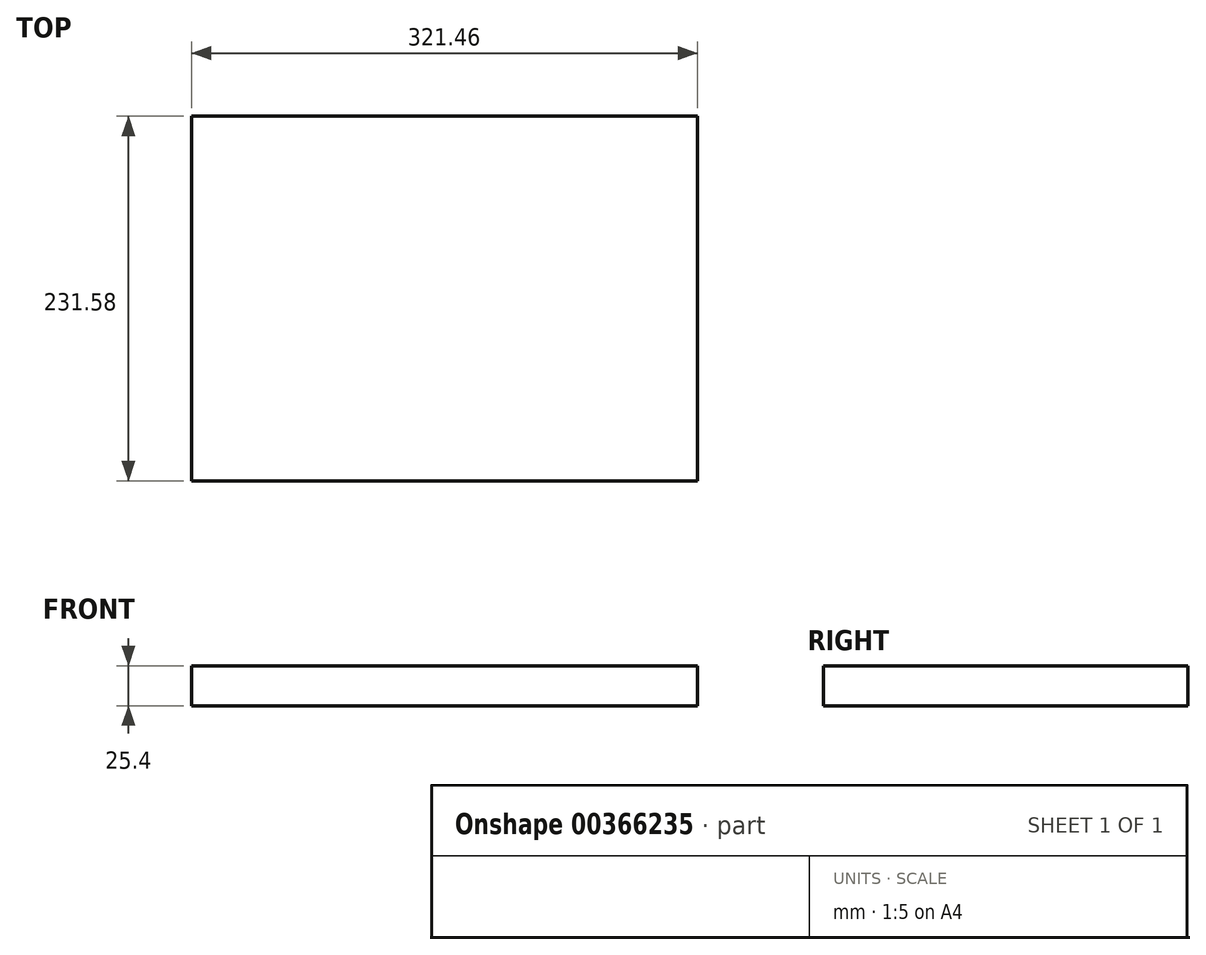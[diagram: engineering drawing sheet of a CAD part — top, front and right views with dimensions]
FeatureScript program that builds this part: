
annotation { "Feature Type Name" : "Feature", "Feature Type Description" : "" }
export const myFeature = defineFeature(function(context is Context, id is Id, definition is map)
    precondition{}
    {
        {
            var Q0;
            Q0=qCreatedBy(makeId("Top.planeOp"),FACE);
            var sketch = newSketch(context, id + "F0", { "sketchPlane" : qUnion([Q0])});
            skLineSegment(sketch, "E0.bottom", {"start": v(-75.95, 128.57) * mm, "end": v(245.51, 128.57) * mm});
            skLineSegment(sketch, "E0.top", {"start": v(-75.95, -103.01) * mm, "end": v(245.51, -103.01) * mm});
            skLineSegment(sketch, "E0.left", {"start": v(-75.95, 128.57) * mm, "end": v(-75.95, -103.01) * mm});
            skLineSegment(sketch, "E0.right", {"start": v(245.51, 128.57) * mm, "end": v(245.51, -103.01) * mm});
            skSolve(sketch);
        }
        {
            var Q0;
            Q0 = qSketchRegion(id + "F0", true);
            extrude(context, id + "F1", {"entities" : qUnion([Q0]), "depth" : 25.4 * mm});
        }
    });
